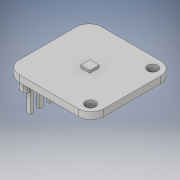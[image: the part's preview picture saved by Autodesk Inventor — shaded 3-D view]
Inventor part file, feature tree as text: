
AUTODESK INVENTOR PART (.ipt)
format: ipt  version: 2018 (Build 220112000, 112)  size: 228,352 bytes
history: native  units: in
note: dims shown in document units (in); Inventor stores cm internally (conversion verified against a paired STEP export)
features: extrude x4, sketch x4, chamfer x1
ambient origin geometry x8: Origin, YZ Plane, XZ Plane, XY Plane, X Axis, Y Axis, Z Axis, Center Point
bodies: Solid1 (feature_tree)
feature tree (9):
  extrude  "Extrusion1"  Depth=0.82in
  extrude  "Extrusion2"  Depth=0.098in
  extrude  "Extrusion3"  Depth=0.05in
  extrude  "Extrusion4"  Depth=0.125in
  chamfer  "Chamfer1"  Distance=0.125in
  sketch  "Sketch1"  dims[d0=0.8in d1=0.82in]
  sketch  "Sketch2"  dims[d2=0.098in d3=0.098in]
  sketch  "Sketch3"  dims[d4=0.055in d5=0.05in]
  sketch  "Sketch4"  dims[d6=0.05in d7=0.055in d8=0.125in d9=0.065in d10=0.0in d11=0.09in d12=0.09in d13=0.023in d14=0.0in d15=0.035in d16=0.035in d17=0.157in d18=0.066in d19=0.03in d20=0.1in d21=0.0in d22=0.033in d23=0.033in d24=2.7559in d26=0.093in d27=0.3937in d29=1.0in d31=0.23in d32=0.0in d33=0.01in d34=0.125in d35=45.0deg]
